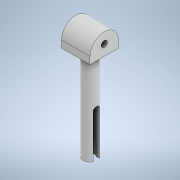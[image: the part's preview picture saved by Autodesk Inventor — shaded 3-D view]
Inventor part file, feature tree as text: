
AUTODESK INVENTOR PART (.ipt)
format: ipt  version: 2022 (Build 260153000, 153)  size: 152,576 bytes
history: native  units: mm
features: extrude x5, sketch x5, fillet x1
ambient origin geometry x8: Origin, YZ Plane, XZ Plane, XY Plane, X Axis, Y Axis, Z Axis, Center Point
bodies: Solid1 (feature_tree)
feature tree (11):
  extrude  "Extrusion1"  Depth=33.0mm TaperAngle=0.0deg
  extrude  "Extrusion2"  Depth=5.0mm
  fillet  "Fillet1"  Radius=5.0mm
  extrude  "Extrusion3"  Depth=5.0mm
  extrude  "Extrusion5"  TaperAngle=0.0deg  [1 undecoded]
  extrude  "Extrusion6"  Depth=5.0mm TaperAngle=0.0deg
  sketch  "Sketch1"  dims[d0=4.8mm d1=33.0mm d2=0.0mm]
  sketch  "Sketch2"  dims[d4=10.0mm d5=5.0mm d6=5.0mm]
  sketch  "Sketch3"  dims[d7=7.5mm d8=0.0mm d9=5.0mm]
  sketch  "Sketch5"  dims[d10=2.2mm d11=0.0mm d12=0.0mm]
  sketch  "Sketch6"  dims[d19=3.0mm d20=5.0mm d21=0.0mm d22=1.0mm d23=8.0mm d24=2.1mm d25=0.0mm d26=0.0mm]
note: 1 required parameter value undecoded (feature->parameter linkage not recoverable at this tier; creation-order binding heuristic only, values carry confidence <= 0.55)
